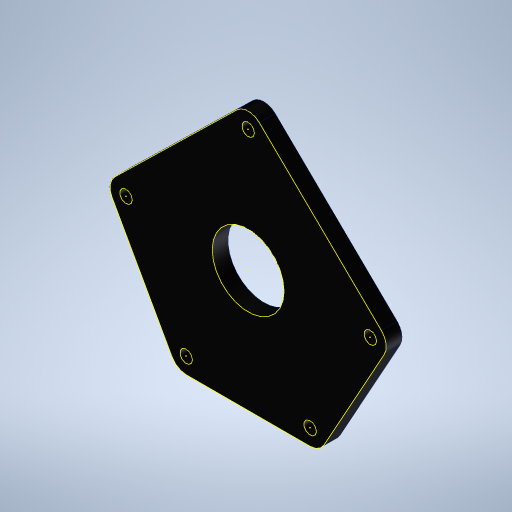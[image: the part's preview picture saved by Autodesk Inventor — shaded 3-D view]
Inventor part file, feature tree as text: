
AUTODESK INVENTOR PART (.ipt)
format: ipt  version: 2024 (Build 280153000, 153)  size: 291,328 bytes
history: native  units: in
note: dims shown in document units (in); Inventor stores cm internally (conversion verified against a paired STEP export)
features: sketch x2, extrude x1, projected_geometry x1
ambient origin geometry x8: Origin, YZ Plane, XZ Plane, XY Plane, X Axis, Y Axis, Z Axis, Center Point
bodies: Body1 (feature_tree)
feature tree (4):
  extrude  "Extrusion2"  Depth=0.1in
  sketch  "Sketch2"  dims[d2=1.125in d3=2.367in d4=2.0in d5=0.6in d12=0.5in d14=0.196in d15=0.313in d16=0.063in d17=0.6in d18=0.8125in d19=0.8125in d32=0.25in d33=0.0in d34=0.5in d35=0.0344in]
  sketch  "Sketch1"  dims[d0=3.0in d1=0.1in]
  projected_geometry  "Projected Loop1"
